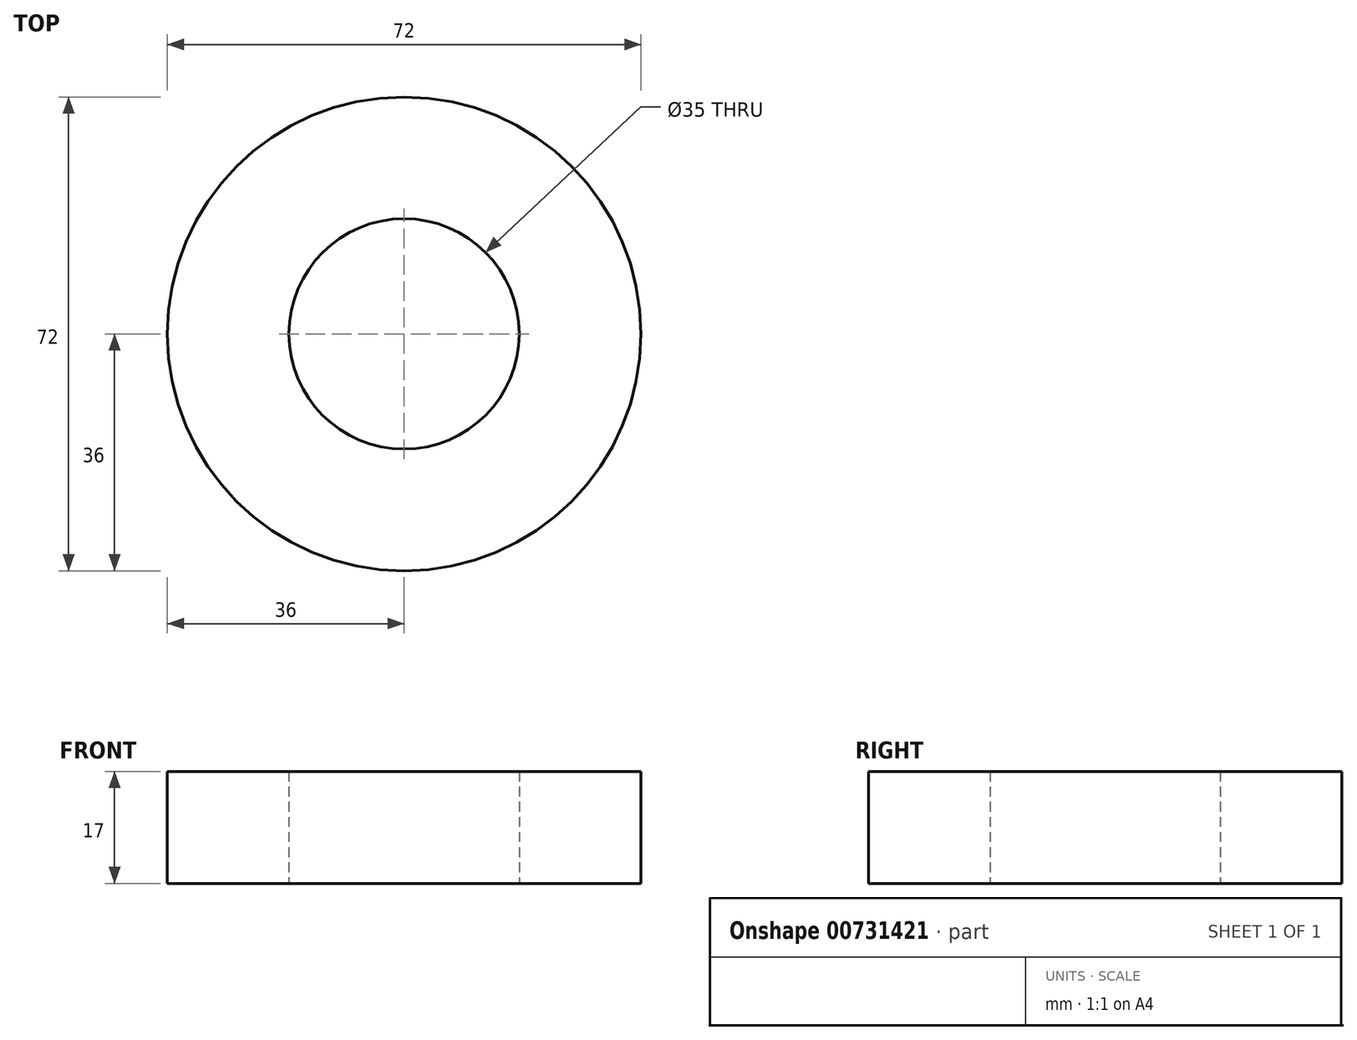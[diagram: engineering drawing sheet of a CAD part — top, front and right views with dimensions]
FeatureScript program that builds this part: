
annotation { "Feature Type Name" : "Feature", "Feature Type Description" : "" }
export const myFeature = defineFeature(function(context is Context, id is Id, definition is map)
    precondition{}
    {
        {
            var Q0;
            Q0=qCreatedBy(makeId("Top.planeOp"),FACE);
            var sketch = newSketch(context, id + "F0", { "sketchPlane" : qUnion([Q0])});
            skCircle(sketch, "E0", {"center": v(0, 0) * mm, "radius": 17.5 * mm});
            skCircle(sketch, "E1", {"center": v(0, 0) * mm, "radius": 36 * mm});
            skSolve(sketch);
        }
        {
            var Q0;
            Q0 = qSketchRegion(id + "F0", true);
            extrude(context, id + "F1", {"entities" : qUnion([Q0]), "depth" : 17 * mm, "offsetDistance" : 25 * mm});
        }
    });
